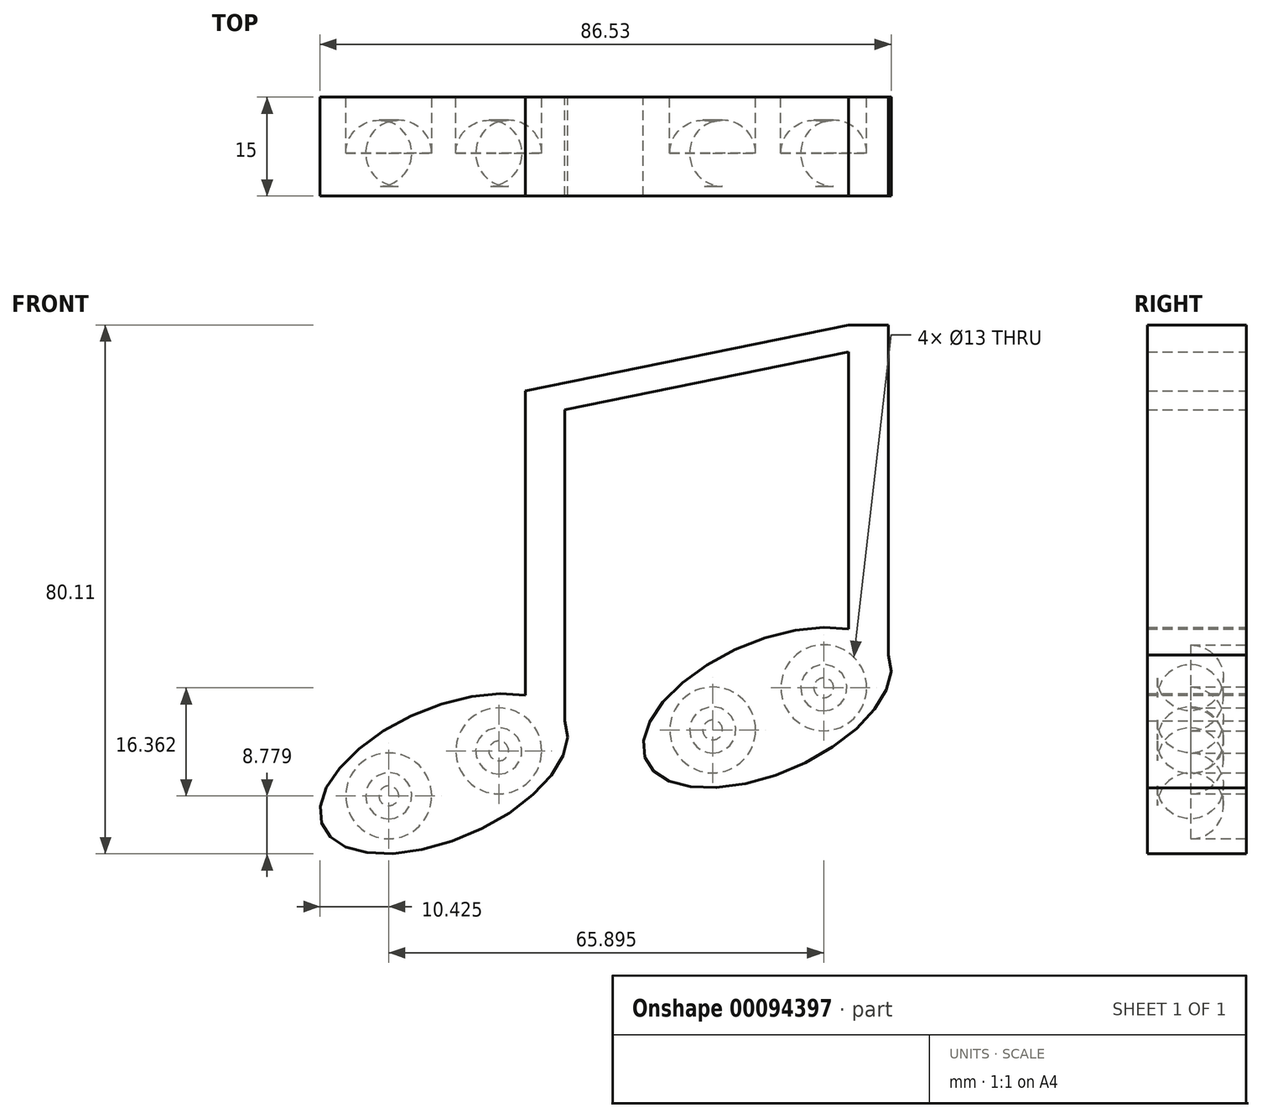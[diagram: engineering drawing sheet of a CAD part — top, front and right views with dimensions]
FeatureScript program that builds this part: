
annotation { "Feature Type Name" : "Feature", "Feature Type Description" : "" }
export const myFeature = defineFeature(function(context is Context, id is Id, definition is map)
    precondition{}
    {
        {
            var Q0;
            Q0=qCreatedBy(makeId("Front.planeOp"),FACE);
            var sketch = newSketch(context, id + "F0", { "sketchPlane" : qUnion([Q0])});
            skEllipse(sketch, "E0", {"center": v(0, 0) * mm, "majorRadius": 20 * mm, "minorRadius": 10 * mm, "majorAxis": v(-0.92, -0.4)});
            skLineSegment(sketch, "E1.bottom", {"start": v(18.35, 7.96) * mm, "end": v(12.35, 7.96) * mm});
            skLineSegment(sketch, "E1.top", {"start": v(18.35, 57.96) * mm, "end": v(12.35, 57.96) * mm});
            skLineSegment(sketch, "E1.left", {"start": v(18.35, 7.96) * mm, "end": v(18.35, 57.96) * mm});
            skLineSegment(sketch, "E1.right", {"start": v(12.35, 7.96) * mm, "end": v(12.35, 57.96) * mm});
            skPoint(sketch, "E2.endSnap0", {"position": v(18.35, 32.96) * mm});
            skEllipse(sketch, "E3", {"center": v(48.99, 10) * mm, "majorRadius": 20 * mm, "minorRadius": 10 * mm, "majorAxis": v(-0.92, -0.4)});
            skLineSegment(sketch, "E4.bottom", {"start": v(67.34, 17.96) * mm, "end": v(61.34, 17.96) * mm});
            skLineSegment(sketch, "E4.top", {"start": v(67.34, 67.96) * mm, "end": v(61.34, 67.96) * mm});
            skLineSegment(sketch, "E4.left", {"start": v(67.34, 17.96) * mm, "end": v(67.34, 67.96) * mm});
            skLineSegment(sketch, "E4.right", {"start": v(61.34, 17.96) * mm, "end": v(61.34, 67.96) * mm});
            skPoint(sketch, "E5.endSnap0", {"position": v(67.34, 42.96) * mm});
            skLineSegment(sketch, "E6", {"start": v(0, 0) * mm, "end": v(115.83, 0) * mm, "construction": true});
            skLineSegment(sketch, "E7", {"start": v(12.35, 57.96) * mm, "end": v(61.34, 67.96) * mm});
            skLineSegment(sketch, "E8", {"start": v(18.35, 55.1) * mm, "end": v(61.34, 63.88) * mm});
            skSolve(sketch);
        }
        {
            var Q0;
            {var subQ0=sQuery(id+"F0.wireOp",EDGE,"E1.bottom");Q0=makeQuery(id+"F0.imprint","IMPRINT",FACE,{"disambiguationData":[TD([[makeQuery(id+"F0.imprint","IMPRINT",EDGE,{"derivedFrom":subQ0}),1.0]])]});}
            var Q1;
            {var subQ0=sQuery(id+"F0.wireOp",EDGE,"E1.bottom");Q1=makeQuery(id+"F0.imprint","IMPRINT",FACE,{"disambiguationData":[TD([[makeQuery(id+"F0.imprint","IMPRINT",EDGE,{"derivedFrom":subQ0}),-1.0]])]});}
            var Q2;
            {var subQ1=sQuery(id+"F0.wireOp",EDGE,"E0");var subQ3=sQuery(id+"F0.wireOp",EDGE,"E1.right");var subQ4=makeQuery(id+"F0.imprint","INTERSECT",VERTEX,{"derivedFrom":[subQ1,subQ3]});Q2=makeQuery(id+"F0.imprint","IMPRINT",FACE,{"disambiguationData":[TD([[makeQuery(id+"F0.imprint","IMPRINT",EDGE,{"disambiguationData":[TD([[subQ4,1.0]])],"derivedFrom":subQ1}),-1.0]])]});}
            var Q3;
            {var subQ0=sQuery(id+"F0.wireOp",EDGE,"E1.top");Q3=makeQuery(id+"F0.imprint","IMPRINT",FACE,{"disambiguationData":[TD([[makeQuery(id+"F0.imprint","IMPRINT",EDGE,{"derivedFrom":subQ0}),1.0]])]});}
            var Q4;
            {var subQ0=sQuery(id+"F0.wireOp",EDGE,"E1.top");Q4=makeQuery(id+"F0.imprint","IMPRINT",FACE,{"disambiguationData":[TD([[makeQuery(id+"F0.imprint","IMPRINT",EDGE,{"derivedFrom":subQ0}),-1.0]])]});}
            var Q5;
            {var subQ0=sQuery(id+"F0.wireOp",EDGE,"E4.left");Q5=makeQuery(id+"F0.imprint","IMPRINT",FACE,{"disambiguationData":[TD([[makeQuery(id+"F0.imprint","IMPRINT",EDGE,{"derivedFrom":subQ0}),1.0]])]});}
            var Q6;
            {var subQ0=sQuery(id+"F0.wireOp",EDGE,"E4.top");Q6=makeQuery(id+"F0.imprint","IMPRINT",FACE,{"disambiguationData":[TD([[makeQuery(id+"F0.imprint","IMPRINT",EDGE,{"derivedFrom":subQ0}),1.0]])]});}
            var Q7;
            {var subQ0=sQuery(id+"F0.wireOp",EDGE,"E4.bottom");Q7=makeQuery(id+"F0.imprint","IMPRINT",FACE,{"disambiguationData":[TD([[makeQuery(id+"F0.imprint","IMPRINT",EDGE,{"derivedFrom":subQ0}),-1.0]])]});}
            var Q8;
            {var subQ0=sQuery(id+"F0.wireOp",EDGE,"E4.bottom");Q8=makeQuery(id+"F0.imprint","IMPRINT",FACE,{"disambiguationData":[TD([[makeQuery(id+"F0.imprint","IMPRINT",EDGE,{"derivedFrom":subQ0}),1.0]])]});}
            extrude(context, id + "F1", {"entities" : qUnion([Q0, Q1, Q2, Q3, Q4, Q5, Q6, Q7, Q8]), "depth" : 15 * mm});
        }
        {
            var Q0;
            Q0=makeQuery(id+"F1.opExtrude","CAP_FACE",FACE,{"disambiguationData":[OSD([sQuery(id+"F0.wireOp",EDGE,"E0"),sQuery(id+"F0.wireOp",EDGE,"E1.left"),sQuery(id+"F0.wireOp",EDGE,"E1.right"),sQuery(id+"F0.wireOp",EDGE,"E3"),sQuery(id+"F0.wireOp",EDGE,"E4.top"),sQuery(id+"F0.wireOp",EDGE,"E4.left"),sQuery(id+"F0.wireOp",EDGE,"E4.right"),sQuery(id+"F0.wireOp",EDGE,"E7"),sQuery(id+"F0.wireOp",EDGE,"E8")])],"isStart":true});
            var sketch = newSketch(context, id + "F2", { "sketchPlane" : qUnion([Q0])});
            skCircle(sketch, "E9", {"center": v(-57.55, 13) * mm, "radius": 6.5 * mm});
            skCircle(sketch, "E10", {"center": v(-40.72, 6.6) * mm, "radius": 6.5 * mm});
            skCircle(sketch, "E11", {"center": v(-8.32, 3.43) * mm, "radius": 6.5 * mm});
            skCircle(sketch, "E12", {"center": v(8.34, -3.37) * mm, "radius": 6.5 * mm});
            skLineSegment(sketch, "E13", {"start": v(0, 0) * mm, "end": v(40.51, -16.37) * mm, "construction": true});
            skLineSegment(sketch, "E14", {"start": v(0, 0) * mm, "end": v(0, 41.2) * mm, "construction": true});
            skSolve(sketch);
        }
        {
            var Q0;
            Q0=makeQuery(id+"F2.imprint","IMPRINT",FACE,{"disambiguationData":[TD([[makeQuery(id+"F2.imprint","IMPRINT",EDGE,{"derivedFrom":sQuery(id+"F2.wireOp",EDGE,"E9")}),1.0]])]});
            var Q1;
            Q1=makeQuery(id+"F2.imprint","IMPRINT",FACE,{"disambiguationData":[TD([[makeQuery(id+"F2.imprint","IMPRINT",EDGE,{"derivedFrom":sQuery(id+"F2.wireOp",EDGE,"E10")}),1.0]])]});
            var Q2;
            Q2=makeQuery(id+"F2.imprint","IMPRINT",FACE,{"disambiguationData":[TD([[makeQuery(id+"F2.imprint","IMPRINT",EDGE,{"derivedFrom":sQuery(id+"F2.wireOp",EDGE,"E11")}),1.0]])]});
            var Q3;
            Q3=makeQuery(id+"F2.imprint","IMPRINT",FACE,{"disambiguationData":[TD([[makeQuery(id+"F2.imprint","IMPRINT",EDGE,{"derivedFrom":sQuery(id+"F2.wireOp",EDGE,"E12")}),1.0]])]});
            extrude(context, id + "F3", {"entities" : qUnion([Q0, Q1, Q2, Q3]), "operationType" : NewBodyOperationType.REMOVE, "oppositeDirection" : true, "depth" : 13.5 * mm});
        }
        {
            var Q0;
            Q0=makeQuery(id+"F3.boolean.opBoolean","COPY",EDGE,{"derivedFrom":makeQuery(id+"F3.opExtrude","CAP_EDGE",EDGE,{"disambiguationData":[OSD([sQuery(id+"F2.wireOp",EDGE,"E10")])],"isStart":false})});
            var Q1;
            Q1=makeQuery(id+"F3.boolean.opBoolean","COPY",EDGE,{"derivedFrom":makeQuery(id+"F3.opExtrude","CAP_EDGE",EDGE,{"disambiguationData":[OSD([sQuery(id+"F2.wireOp",EDGE,"E9")])],"isStart":false})});
            var Q2;
            Q2=makeQuery(id+"F3.boolean.opBoolean","COPY",FACE,{"derivedFrom":makeQuery(id+"F3.opExtrude","CAP_FACE",FACE,{"disambiguationData":[OSD([sQuery(id+"F2.wireOp",EDGE,"E11")])],"isStart":false})});
            var Q3;
            Q3=makeQuery(id+"F3.boolean.opBoolean","COPY",FACE,{"derivedFrom":makeQuery(id+"F3.opExtrude","CAP_FACE",FACE,{"disambiguationData":[OSD([sQuery(id+"F2.wireOp",EDGE,"E12")])],"isStart":false})});
            fillet(context, id + "F4", {"entities" : qUnion([Q0, Q1, Q2, Q3]), "radius" : 5 * mm, "tangentPropagation" : true, "allowEdgeOverflow" : false});
        }
    });
